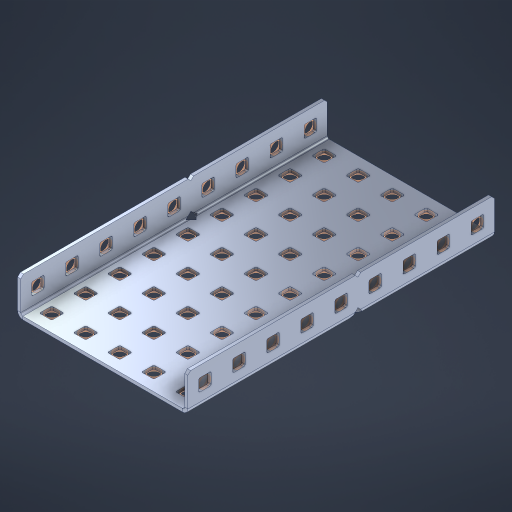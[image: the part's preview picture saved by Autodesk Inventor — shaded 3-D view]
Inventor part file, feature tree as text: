
AUTODESK INVENTOR PART (.ipt)
format: ipt  version: 2023 (Build 270158000, 158)  size: 967,168 bytes
history: native  units: in
note: dims shown in document units (in); Inventor stores cm internally (conversion verified against a paired STEP export)
features: other x68, extrude x62, sheet_metal_op x10, sketch x8, mirror x1, pattern_linear x1, chamfer x1
ambient origin geometry x8: Origin, YZ Plane, XZ Plane, XY Plane, X Axis, Y Axis, Z Axis, Center Point
bodies: Solid1 (feature_tree), Body (feature_tree)
feature tree (151):
  other  "Flange Pattern Plane"
  sheet_metal_op  "Flange Pattern"
  sheet_metal_op  "Body Pattern"
  other  "Arc Length"
  mirror  "Notch Mirror"
  pattern_linear  "Notch Pattern"  Spacing1=0.1875in  [1 undecoded]
  chamfer  "End Chamfer"
  extrude  "Half Cut"  Depth=0.0469in
  sketch  "Sketch1"  dims[d0=2.5in]
  other  "Plate1"
  sketch  "Sketch2"  dims[d1=4.5in]
  other  "Plate2"
  sheet_metal_op  "Bend1"
  sheet_metal_op  "Corner1"
  sketch  "Sketch3"  dims[d2=0.0469in]
  other  "Flange Pattern Sketch"
  sketch  "Sketch7"  dims[d3=0.0469in]
  other  "Srf1"
  other  "Srf2"
  sketch  "Sketch8"  dims[d4=0.0234in]
  sketch  "Sketch9"  dims[d5=0.0938in]
  other  "Srf91"
  sheet_metal_op  "Body Pattern Sketch"
  other  "Srf92"
  sketch  "Sketch13"  dims[d6=0.0469in]
  sketch  "Sketch14"  dims[d7=0.5in d8=90.0deg d9=0.0312in d10=0.1875in d11=0.0469in d12=0.0469in d16=0.182in d17=0.02in d18=0.0469in d19=0.0in d20=0.25in d21=0.25in d46=0.172in d47=1.0in d48=0.0in d49=0.182in d50=0.02in d51=0.25in d52=0.25in d53=0.0469in d54=0.0in d55=0.172in d56=1.0in d57=0.0in d60=3.5433in d62=0.5in d63=1.9685in d65=0.5in d85=0.1227in d86=0.1659in d88=0.04in d89=0.0469in d90=0.0in d91=0.04in d92=0.0491in d95=2.5in d96=0.04in d97=0.25in d98=45.0deg d101=0.0in d102=2.497in d131=2.5in d132=3.5433in d134=0.5in d139=0.5in]
  other  "Srf856"
  other  "Srf1310"
  other  "Srf1311"
  other  "Srf1312"
  other  "Srf1376"
  other  "Srf1377"
  other  "Srf1728"
  other  "Srf1755"
  other  "Srf1878"
  other  "Srf1879"
  other  "Srf1880"
  other  "Srf1881"
  other  "Srf1882"
  other  "Srf1883"
  other  "Srf1884"
  other  "Srf1885"
  other  "Srf1886"
  other  "Srf1887"
  other  "Srf1888"
  other  "Srf1889"
  other  "Srf1942"
  other  "Srf1943"
  other  "Srf1944"
  other  "Srf1945"
  other  "Srf1946"
  other  "Srf1947"
  other  "Srf1948"
  other  "Srf1949"
  other  "Srf1950"
  other  "Srf1951"
  other  "Srf1952"
  other  "Srf1953"
  other  "Srf1954"
  other  "Srf1955"
  other  "Srf1956"
  other  "Srf1957"
  other  "Srf1958"
  other  "Srf1959"
  other  "Srf1960"
  other  "Srf1961"
  other  "Srf1962"
  other  "Srf1963"
  other  "Srf1964"
  other  "Srf1965"
  other  "Srf1966"
  other  "Srf1967"
  other  "Srf1968"
  other  "Srf1969"
  other  "Srf1970"
  other  "Srf2146"
  other  "Srf2147"
  other  "Srf2148"
  other  "Srf2149"
  other  "Srf2150"
  other  "Srf2151"
  other  "Srf2152"
  other  "Srf2153"
  other  "Srf2154"
  other  "Srf2155"
  sheet_metal_op  "Flange Stamp"
  sheet_metal_op  "Flange Circle"
  sheet_metal_op  "Body Stamp"
  sheet_metal_op  "Body Circle"
  sheet_metal_op  "Notch"
  extrude  "ExtrusionSrf2"  Depth=0.0469in
  extrude  "ExtrusionSrf92"  Depth=2.5in
  extrude  "ExtrusionSrf856"  Depth=0.02in
  extrude  "ExtrusionSrf1310"  Depth=0.0469in
  extrude  "ExtrusionSrf1311"  TaperAngle=0.0deg  [1 undecoded]
  extrude  "ExtrusionSrf1312"  Depth=0.25in
  extrude  "ExtrusionSrf1376"  Depth=0.25in
  extrude  "ExtrusionSrf1377"  Depth=2.5in
  extrude  "ExtrusionSrf1728"  Depth=2.5in TaperAngle=0.0deg
  extrude  "ExtrusionSrf1755"  Depth=2.5in
  extrude  "ExtrusionSrf1878"  Depth=0.02in
  extrude  "ExtrusionSrf1879"  Depth=0.25in
  extrude  "ExtrusionSrf1880"  Depth=0.25in
  extrude  "ExtrusionSrf1881"  Depth=0.0469in
  extrude  "ExtrusionSrf1882"  TaperAngle=0.0deg  [1 undecoded]
  extrude  "ExtrusionSrf1883"  Depth=2.5in
  extrude  "ExtrusionSrf1884"  Depth=2.5in TaperAngle=0.0deg
  extrude  "ExtrusionSrf1885"  Depth=2.5in
  extrude  "ExtrusionSrf1886"  Depth=2.5in
  extrude  "ExtrusionSrf1887"  Depth=2.5in
  extrude  "ExtrusionSrf1888"  Depth=2.5in
  extrude  "ExtrusionSrf1889"  Depth=2.5in
  extrude  "ExtrusionSrf1942"  Depth=0.0469in
  extrude  "ExtrusionSrf1943"  TaperAngle=0.0deg  [1 undecoded]
  extrude  "ExtrusionSrf1944"  Depth=2.5in
  extrude  "ExtrusionSrf1945"  Depth=2.5in
  extrude  "ExtrusionSrf1946"  Depth=2.5in
  extrude  "ExtrusionSrf1947"  Depth=0.25in TaperAngle=45.0deg
  extrude  "ExtrusionSrf1948"  TaperAngle=0.0deg  [1 undecoded]
  extrude  "ExtrusionSrf1949"  Depth=2.5in
  extrude  "ExtrusionSrf1950"  Depth=2.5in
  extrude  "ExtrusionSrf1951"  Depth=2.5in
  extrude  "ExtrusionSrf1952"  Depth=2.5in
  extrude  "ExtrusionSrf1953"  Depth=2.5in
  extrude  "ExtrusionSrf1954"  [1 undecoded]
  extrude  "ExtrusionSrf1955"  [1 undecoded]
  extrude  "ExtrusionSrf1956"  [1 undecoded]
  extrude  "ExtrusionSrf1957"  [1 undecoded]
  extrude  "ExtrusionSrf1958"  [1 undecoded]
  extrude  "ExtrusionSrf1959"  [1 undecoded]
  extrude  "ExtrusionSrf1960"  [1 undecoded]
  extrude  "ExtrusionSrf1961"  [1 undecoded]
  extrude  "ExtrusionSrf1962"  [1 undecoded]
  extrude  "ExtrusionSrf1963"  [1 undecoded]
  extrude  "ExtrusionSrf1964"  [1 undecoded]
  extrude  "ExtrusionSrf1965"  [1 undecoded]
  extrude  "ExtrusionSrf1966"  [1 undecoded]
  extrude  "ExtrusionSrf1967"  [1 undecoded]
  extrude  "ExtrusionSrf1968"  [1 undecoded]
  extrude  "ExtrusionSrf1969"  [1 undecoded]
  extrude  "ExtrusionSrf1970"  [1 undecoded]
  extrude  "ExtrusionSrf2146"  [1 undecoded]
  extrude  "ExtrusionSrf2147"  [1 undecoded]
  extrude  "ExtrusionSrf2148"  [1 undecoded]
  extrude  "ExtrusionSrf2149"  [1 undecoded]
  extrude  "ExtrusionSrf2150"  [1 undecoded]
  extrude  "ExtrusionSrf2151"  [1 undecoded]
  extrude  "ExtrusionSrf2152"  [1 undecoded]
  extrude  "ExtrusionSrf2153"  [1 undecoded]
  extrude  "ExtrusionSrf2154"  [1 undecoded]
  extrude  "ExtrusionSrf2155"  [1 undecoded]
note: 32 required parameter values undecoded (feature->parameter linkage not recoverable at this tier; creation-order binding heuristic only, values carry confidence <= 0.55)
